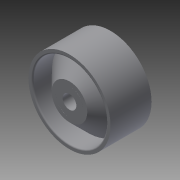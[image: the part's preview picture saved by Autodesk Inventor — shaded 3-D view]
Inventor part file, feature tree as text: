
AUTODESK INVENTOR PART (.ipt)
format: ipt  version: 2014 (Build 180170000, 170)  size: 143,360 bytes
history: native  units: mm
features: extrude x4, sketch x2, chamfer x2, fillet x2
ambient origin geometry x8: Origin, YZ Plane, XZ Plane, XY Plane, X Axis, Y Axis, Z Axis, Center Point
bodies: Solid1 (feature_tree), Solid2 (feature_tree), Solid3 (feature_tree)
feature tree (10):
  sketch  "Sketch1"  dims[d0=30.0mm d1=27.0mm]
  extrude  "Extrusion1"  Depth=27.0mm
  extrude  "Extrusion3"  Depth=15.0mm TaperAngle=0.0deg
  chamfer  "Chamfer1"  Distance=15.0mm
  chamfer  "Chamfer2"  Distance=7.0mm Angle=45.0deg
  fillet  "Fillet1"  Radius=5.0mm
  fillet  "Fillet2"  Radius=0.5mm
  extrude  "Extrusion4"  Depth=0.5mm
  extrude  "Extrusion5"  Depth=15.0mm TaperAngle=0.0deg
  sketch  "Sketch2"  dims[d2=10.0mm d3=15.0mm d4=0.0mm d7=15.0mm d8=0.0mm d9=7.0mm d10=2.0mm d11=45.0deg d12=7.0mm d13=5.0mm d14=45.0deg d15=0.5mm d16=0.5mm d17=15.0mm d18=0.0mm d19=5.0mm d20=15.0mm d21=0.0mm]
